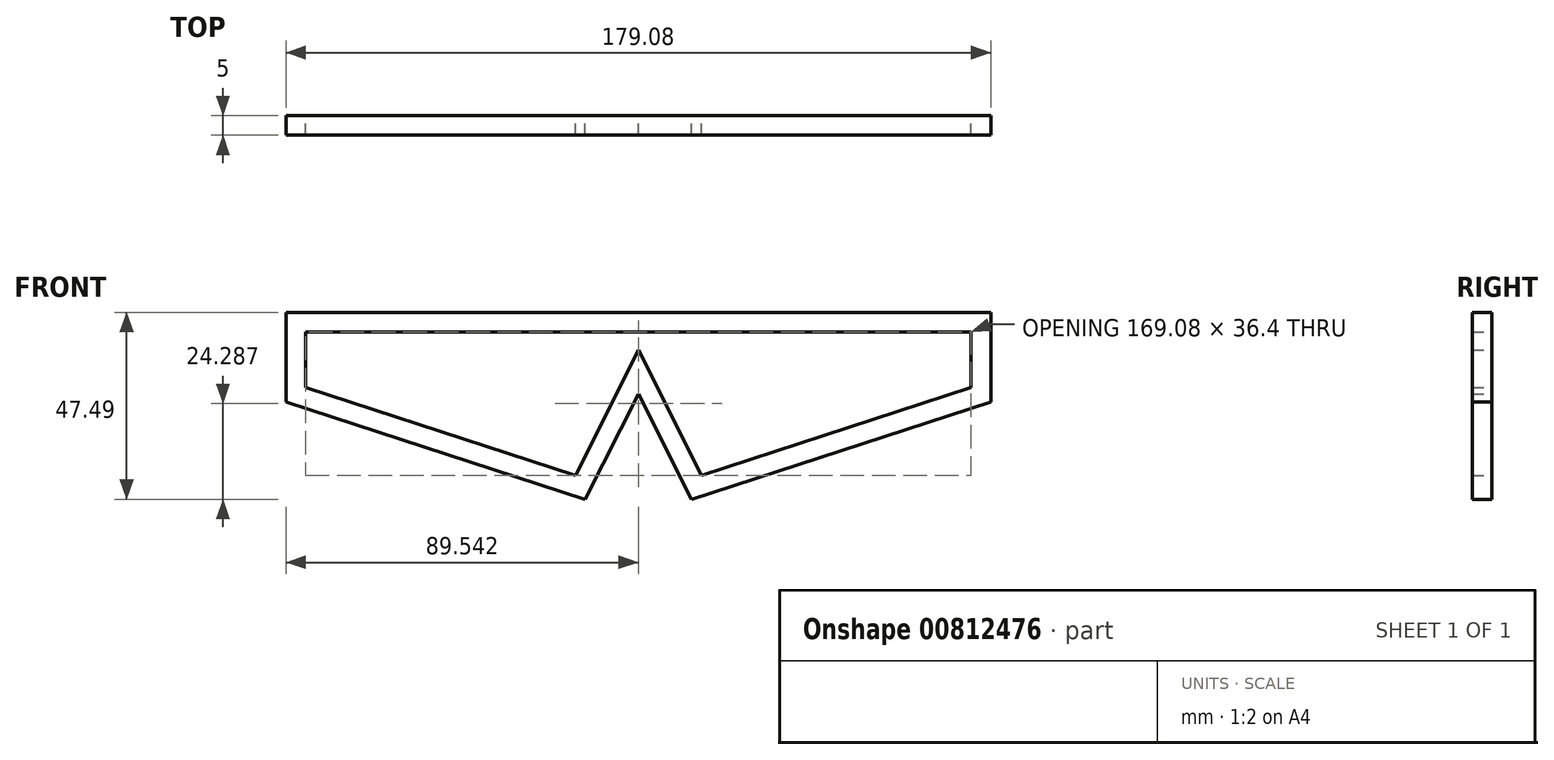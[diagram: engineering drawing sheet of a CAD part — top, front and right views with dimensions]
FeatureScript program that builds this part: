
annotation { "Feature Type Name" : "Feature", "Feature Type Description" : "" }
export const myFeature = defineFeature(function(context is Context, id is Id, definition is map)
    precondition{}
    {
        {
            var Q0;
            Q0=qCreatedBy(makeId("Front.planeOp"),FACE);
            var sketch = newSketch(context, id + "F0", { "sketchPlane" : qUnion([Q0])});
            skLineSegment(sketch, "E0.top", {"start": v(0.53, 47.34) * mm, "end": v(-89, 47.34) * mm});
            skLineSegment(sketch, "E0.right", {"start": v(-89, 24.64) * mm, "end": v(-89, 47.34) * mm});
            skLineSegment(sketch, "E1", {"start": v(-12.95, -0.15) * mm, "end": v(0.53, 26.65) * mm});
            skLineSegment(sketch, "E2", {"start": v(-12.95, -0.15) * mm, "end": v(-89, 24.64) * mm});
            skLineSegment(sketch, "E3.MirrorCS", {"start": v(14, -0.15) * mm, "end": v(0.53, 26.65) * mm});
            skLineSegment(sketch, "E4.MirrorCS", {"start": v(14, -0.15) * mm, "end": v(90.07, 24.64) * mm});
            skLineSegment(sketch, "E5.MirrorCS", {"start": v(90.07, 24.64) * mm, "end": v(90.07, 47.34) * mm});
            skLineSegment(sketch, "E6.MirrorCS", {"start": v(0.53, 47.34) * mm, "end": v(90.07, 47.34) * mm});
            skSolve(sketch);
        }
        {
            var Q0;
            Q0=makeQuery(id+"F0.imprint","IMPRINT",FACE,{"disambiguationData":[TD([[makeQuery(id+"F0.imprint","IMPRINT",EDGE,{"derivedFrom":sQuery(id+"F0.wireOp",EDGE,"E0.top")}),1.0]])]});
            extrude(context, id + "F1", {"entities" : qUnion([Q0]), "depth" : 150 * mm, "offsetDistance" : 25 * mm});
        }
        {
            var Q0;
            Q0=qCreatedBy(makeId("Front.planeOp"),FACE);
            var sketch = newSketch(context, id + "F2", { "sketchPlane" : qUnion([Q0])});
            skLineSegment(sketch, "E7.0", {"start": v(0.53, 37.78) * mm, "end": v(16.55, 5.94) * mm});
            skLineSegment(sketch, "E7.1", {"start": v(-15.48, 5.94) * mm, "end": v(0.53, 37.78) * mm});
            skLineSegment(sketch, "E7.2", {"start": v(85.07, 28.27) * mm, "end": v(85.07, 42.34) * mm});
            skLineSegment(sketch, "E7.3", {"start": v(85.07, 42.34) * mm, "end": v(-84, 42.34) * mm});
            skLineSegment(sketch, "E7.4", {"start": v(-84, 42.34) * mm, "end": v(-84, 28.27) * mm});
            skLineSegment(sketch, "E7.5", {"start": v(16.55, 5.94) * mm, "end": v(85.07, 28.27) * mm});
            skLineSegment(sketch, "E7.6", {"start": v(-84, 28.27) * mm, "end": v(-15.48, 5.94) * mm});
            skSolve(sketch);
        }
        {
            var Q0;
            Q0=makeQuery(id+"F2.imprint","IMPRINT",FACE,{"disambiguationData":[TD([[makeQuery(id+"F2.imprint","IMPRINT",EDGE,{"derivedFrom":sQuery(id+"F2.wireOp",EDGE,"E7.0")}),1.0]])]});
            extrude(context, id + "F3", {"entities" : qUnion([Q0]), "operationType" : NewBodyOperationType.REMOVE, "depth" : 163 * mm, "offsetDistance" : 25 * mm});
        }
        {
            var Q0;
            Q0=makeQuery(id+"F1.opExtrude","CAP_FACE",FACE,{"disambiguationData":[OSD([sQuery(id+"F0.wireOp",EDGE,"E0.top"),sQuery(id+"F0.wireOp",EDGE,"E0.right"),sQuery(id+"F0.wireOp",EDGE,"E1"),sQuery(id+"F0.wireOp",EDGE,"E2"),sQuery(id+"F0.wireOp",EDGE,"E3.MirrorCS"),sQuery(id+"F0.wireOp",EDGE,"E4.MirrorCS"),sQuery(id+"F0.wireOp",EDGE,"E5.MirrorCS"),sQuery(id+"F0.wireOp",EDGE,"E6.MirrorCS")])],"isStart":false});
            extrude(context, id + "F4", {"entities" : qUnion([Q0]), "operationType" : NewBodyOperationType.REMOVE, "oppositeDirection" : true, "depth" : 145 * mm, "offsetDistance" : 25 * mm});
        }
    });
